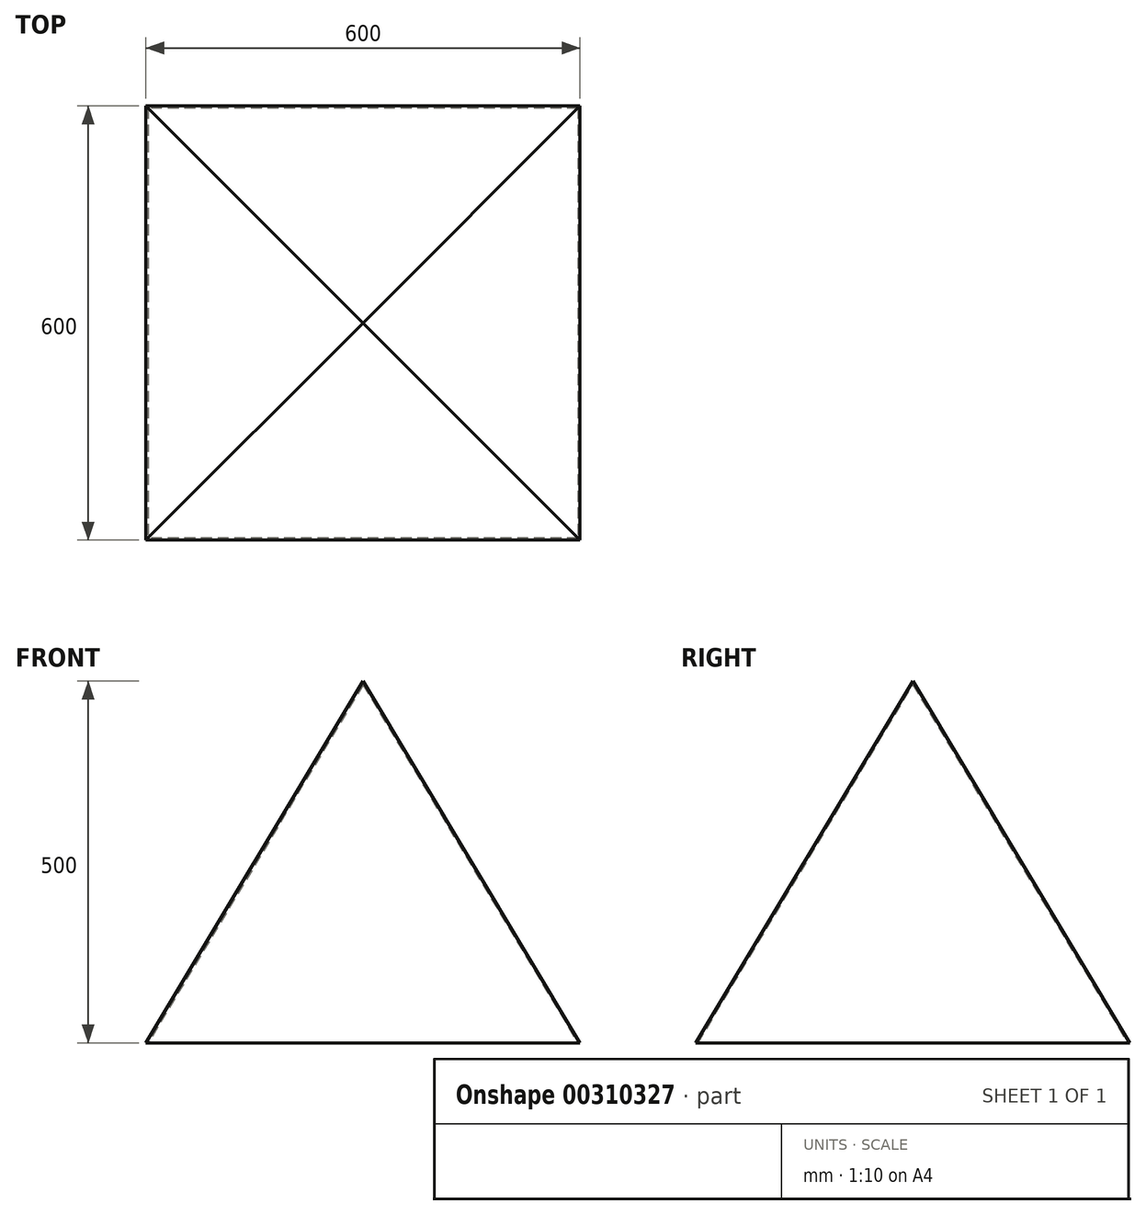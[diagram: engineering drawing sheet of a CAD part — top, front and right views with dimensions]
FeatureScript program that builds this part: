
annotation { "Feature Type Name" : "Feature", "Feature Type Description" : "" }
export const myFeature = defineFeature(function(context is Context, id is Id, definition is map)
    precondition{}
    {
        {
            var Q0;
            Q0=qCreatedBy(makeId("Top.planeOp"),FACE);
            var sketch = newSketch(context, id + "F0", { "sketchPlane" : qUnion([Q0])});
            skLineSegment(sketch, "E0.bottom", {"start": v(300, 300) * mm, "end": v(-300, 300) * mm});
            skLineSegment(sketch, "E0.top", {"start": v(300, -300) * mm, "end": v(-300, -300) * mm});
            skLineSegment(sketch, "E0.left", {"start": v(300, 300) * mm, "end": v(300, -300) * mm});
            skLineSegment(sketch, "E0.right", {"start": v(-300, 300) * mm, "end": v(-300, -300) * mm});
            skPoint(sketch, "E0.middle", {"position": v(0, 0) * mm});
            skSolve(sketch);
        }
        {
            var Q0;
            Q0=qCreatedBy(makeId("Front.planeOp"),FACE);
            var sketch = newSketch(context, id + "F1", { "sketchPlane" : qUnion([Q0])});
            skPoint(sketch, "E1", {"position": v(0, 500) * mm});
            skSolve(sketch);
        }
        {
            var Q0;
            Q0=makeQuery(id+"F0.imprint","IMPRINT",FACE,{"disambiguationData":[TD([[makeQuery(id+"F0.imprint","IMPRINT",EDGE,{"derivedFrom":sQuery(id+"F0.wireOp",EDGE,"E0.bottom")}),1.0]])]});
            var Q1;
            Q1=sQuery(id+"F1.wireOp",VERTEX,"E1");
            loft(context, id + "F2", {"sheetProfilesArray" : [{ "sheetProfileEntities" : qUnion([Q0]) }, { "sheetProfileEntities" : qUnion([Q1]) }]});
        }
        {
            var Q0;
            Q0=makeQuery(id+"F2.opLoft","CAP_FACE",FACE,{"disambiguationData":[OSD([makeQuery(id+"F0.imprint","IMPRINT",FACE,{"disambiguationData":[TD([[makeQuery(id+"F0.imprint","IMPRINT",EDGE,{"derivedFrom":sQuery(id+"F0.wireOp",EDGE,"E0.bottom")}),1.0]])]})])],"isStart":true});
            shell(context, id + "F3", {"entities" : qUnion([Q0]), "thickness" : 2.5 * mm});
        }
    });
